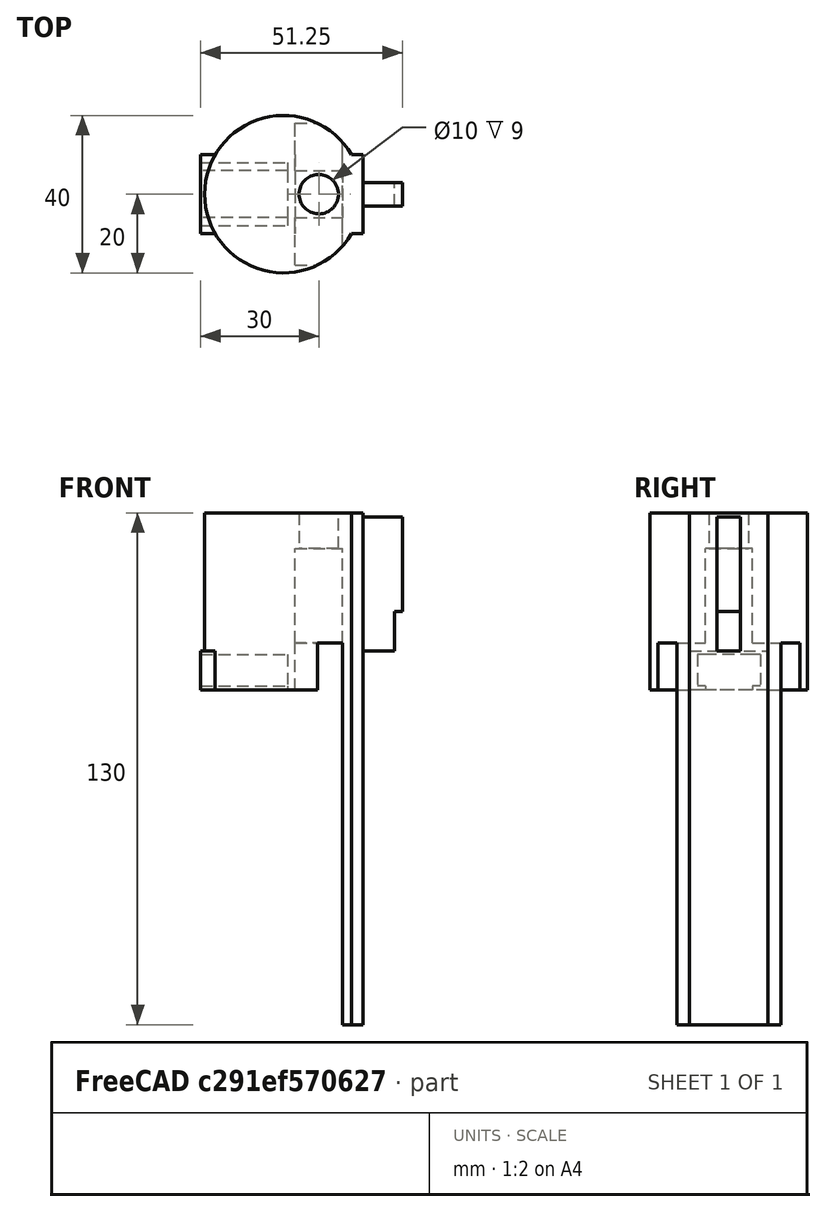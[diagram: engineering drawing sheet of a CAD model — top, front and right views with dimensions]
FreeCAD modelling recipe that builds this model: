
FCSTD DOCUMENT  (FreeCAD 0.20R29410 (Git))
Label: shortBarrel1
License: All rights reserved
LicenseURL: http://en.wikipedia.org/wiki/All_rights_reserved
objects: Part::Box×10, Part::MultiFuse×6, Part::Cut×5, Part::Cylinder×2, Part::Feature×1
note: 24 computed .brp shape members not serialized (recipe doc carries the construction recipe); baked Part::Feature solids carry a one-line shape summary decoded from their .brp

FEATURE [Part::Box] Box004  label="Cube004"
  AttacherType = Attacher::AttachEngine3D
  Height = 24
  Length = 10
  Placement = pos=(27.25,-3,10) rot=(0,0,1;0rad)
  Width = 6
FEATURE [Part::Box] Box005  label="Cube005"
  AttacherType = Attacher::AttachEngine3D
  Height = 34
  Length = 8
  Placement = pos=(27.25,-3,0) rot=(0,0,1;0rad)
  Width = 6
FEATURE [Part::MultiFuse] Fusion002  label="frontSight"
  Placement = pos=(-2,0,95) rot=(0,0,1;0rad)
  Shapes = -> [Box004,Box005]
FEATURE [Part::Box] Box006  label="Cube006"
  AttacherType = Attacher::AttachEngine3D
  Height = 130
  Length = 8
  Placement = pos=(17.25,-10,0) rot=(0,0,1;0rad)
  Width = 20
FEATURE [Part::Cylinder] Cylinder
  Angle = 360
  AttacherType = Attacher::AttachEngine3D
  FirstAngle = 0
  Height = 130
  Radius = 20
  SecondAngle = 0
FEATURE [Part::Cylinder] Cylinder001
  Angle = 360
  AttacherType = Attacher::AttachEngine3D
  FirstAngle = 0
  Height = 130
  Placement = pos=(9,0,8) rot=(0,0,1;0rad)
  Radius = 5
  SecondAngle = 0
FEATURE [Part::MultiFuse] Fusion
  Placement = pos=(-5,0,0) rot=(0,0,1;0rad)
  Shapes = -> [Fusion002,Box006]
FEATURE [Part::MultiFuse] Fusion003
  Shapes = -> [Fusion,Cylinder]
FEATURE [Part::Box] Box  label="Cube"
  AttacherType = Attacher::AttachEngine3D
  Height = 85
  Length = 40
  Placement = pos=(-25,-20,0) rot=(0,0,1;0rad)
  Width = 40
FEATURE [Part::Cut] Cut
  Base = -> Fusion003
  Tool = -> Box
FEATURE [Part::Cut] Cut001
  Base = -> Cut
  Tool = -> Cylinder001
FEATURE [Part::Box] Box007  label="Cube007"
  AttacherType = Attacher::AttachEngine3D
  Height = 12
  Length = 12
  Placement = pos=(3,-18,85) rot=(0,0,1;0rad)
  Width = 36
FEATURE [Part::Box] Box008  label="Cube008"
  AttacherType = Attacher::AttachEngine3D
  Height = 12
  Length = 12
  Placement = pos=(3,6,85) rot=(1,0,0;1.5708rad)
  Width = 36
FEATURE [Part::MultiFuse] Fusion004
  Shapes = -> [Box008,Box007]
FEATURE [Part::Cut] Cut002
  Base = -> Cut001
  Tool = -> Fusion004
FEATURE [Part::Box] Box012  label="Cube012"
  AttacherType = Attacher::AttachEngine3D
  Height = 10
  Length = 24
  Width = 20
FEATURE [Part::Box] Box013  label="Cube013"
  AttacherType = Attacher::AttachEngine3D
  Height = 8
  Length = 22
  Placement = pos=(0,2,1) rot=(0,0,1;0rad)
  Width = 16
FEATURE [Part::Box] Box014  label="Cube014"
  AttacherType = Attacher::AttachEngine3D
  Height = 10
  Length = 22
  Placement = pos=(0,4,1) rot=(0,0,1;0rad)
  Width = 12
FEATURE [Part::MultiFuse] Fusion006
  Shapes = -> [Box014,Box013]
FEATURE [Part::Box] Box015  label="Cube015"
  AttacherType = Attacher::AttachEngine3D
  Height = 10
  Length = 24
  Placement = pos=(-21,-10,85) rot=(0,0,1;0rad)
  Width = 20
FEATURE [Part::Cut] Cut005
  Base = -> Cut002
  Tool = -> Box015
FEATURE [Part::Cut] Cut004
  Base = -> Box012
  Placement = pos=(-21,10,95) rot=(1,0,0;3.14159rad)
  Tool = -> Fusion006
FEATURE [Part::MultiFuse] Fusion007
  Shapes = -> [Cut005,Cut004]
FEATURE [Part::Feature] Fusion007_solid  label="Fusion007 (Solid)"
  shape: bbox 51.25 x 40 x 130 mm, 61 faces (baked)
